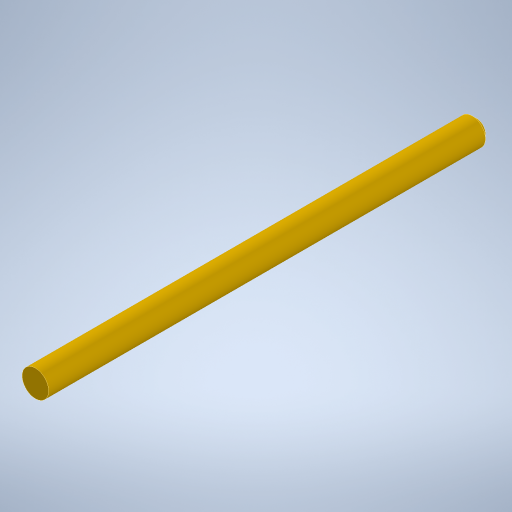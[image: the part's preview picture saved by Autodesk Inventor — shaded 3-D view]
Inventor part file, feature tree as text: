
AUTODESK INVENTOR PART (.ipt)
format: ipt  version: 2024.1 (Build 281209000, 209)  size: 240,128 bytes
history: native  units: in
note: dims shown in document units (in); Inventor stores cm internally (conversion verified against a paired STEP export)
features: extrude x1, chamfer x1, sketch x1
ambient origin geometry x8: Origin, YZ Plane, XZ Plane, XY Plane, X Axis, Y Axis, Z Axis, Center Point
bodies: Solid1 (feature_tree)
feature tree (3):
  extrude  "Extrusion1"  Depth=1.9685in TaperAngle=0.0deg
  chamfer  "Chamfer1"  Distance=0.0197in Angle=45.0deg
  sketch  "Sketch1"  dims[d0=0.1181in d1=1.9685in d2=0.0in d3=0.0197in d4=0.125in d5=45.0deg]
